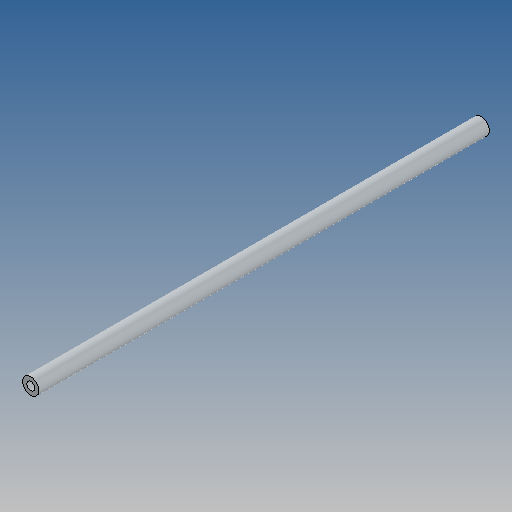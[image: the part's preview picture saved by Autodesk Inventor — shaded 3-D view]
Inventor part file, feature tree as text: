
AUTODESK INVENTOR PART (.ipt)
format: ipt  version: 2025 (Build 290162010, 162A)  size: 84,992 bytes
history: native  units: mm
features: extrude x1, sketch x1
ambient origin geometry x8: Origin, YZ Plane, XZ Plane, XY Plane, X Axis, Y Axis, Z Axis, Center Point
bodies: Volumenkörper1 (feature_tree)
feature tree (2):
  extrude  "Extrusion1"  Depth=1.6mm
  sketch  "Skizze1"  dims[d0=3.2mm d1=1.6mm d2=88.0mm d3=0.0mm]
